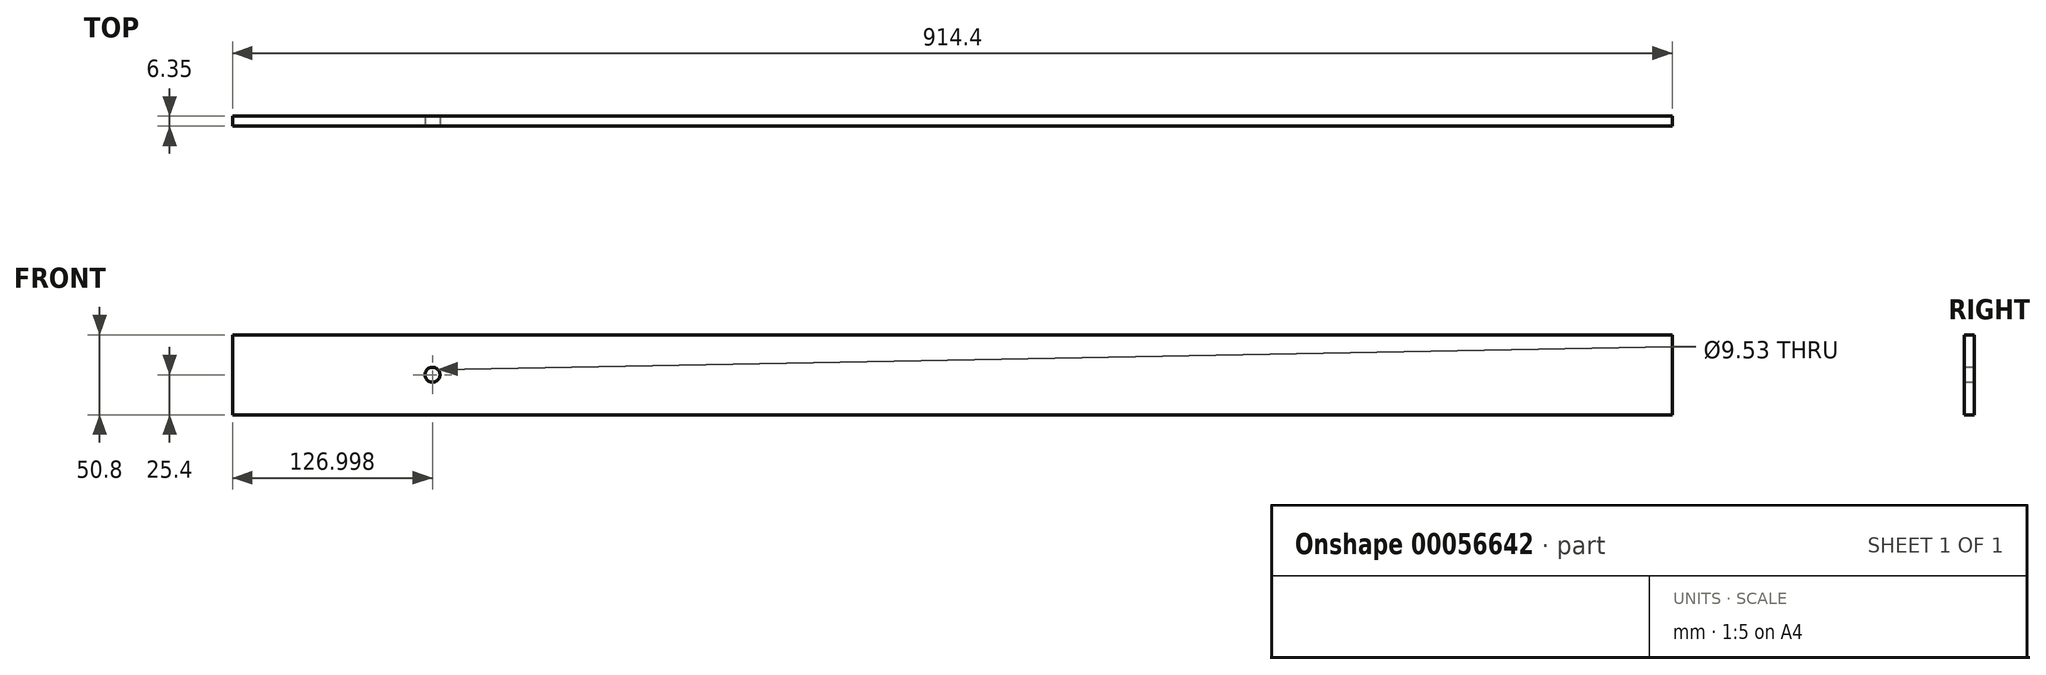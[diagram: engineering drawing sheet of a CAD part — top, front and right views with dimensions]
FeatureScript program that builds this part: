
annotation { "Feature Type Name" : "Feature", "Feature Type Description" : "" }
export const myFeature = defineFeature(function(context is Context, id is Id, definition is map)
    precondition{}
    {
        {
            var Q0;
            Q0=qCreatedBy(makeId("Top.planeOp"),FACE);
            var sketch = newSketch(context, id + "F0", { "sketchPlane" : qUnion([Q0])});
            skLineSegment(sketch, "E0.bottom", {"start": v(-447.68, 17.14) * mm, "end": v(466.72, 17.14) * mm});
            skLineSegment(sketch, "E0.top", {"start": v(-447.68, 10.8) * mm, "end": v(466.72, 10.8) * mm});
            skLineSegment(sketch, "E0.left", {"start": v(-447.68, 17.14) * mm, "end": v(-447.68, 10.8) * mm});
            skLineSegment(sketch, "E0.right", {"start": v(466.72, 17.14) * mm, "end": v(466.72, 10.8) * mm});
            skSolve(sketch);
        }
        {
            var Q0;
            Q0 = qSketchRegion(id + "F0", true);
            extrude(context, id + "F1", {"entities" : qUnion([Q0]), "endBound" : BoundingType.SYMMETRIC, "depth" : 50.8 * mm});
        }
        {
            var Q0;
            Q0=makeQuery(id+"F1.opExtrude","SWEPT_FACE",FACE,{"disambiguationData":[OSD([sQuery(id+"F0.wireOp",EDGE,"E0.top")])]});
            var sketch = newSketch(context, id + "F2", { "sketchPlane" : qUnion([Q0])});
            skCircle(sketch, "E1", {"center": v(-320.68, 0) * mm, "radius": 4.76 * mm});
            skPoint(sketch, "E1.centerSnap0", {"position": v(-447.68, 0) * mm});
            skSolve(sketch);
        }
        {
            var Q0;
            Q0 = qSketchRegion(id + "F2", true);
            extrude(context, id + "F3", {"entities" : qUnion([Q0]), "operationType" : NewBodyOperationType.REMOVE, "endBound" : BoundingType.THROUGH_ALL, "oppositeDirection" : true, "depth" : 25.4 * mm});
        }
    });
